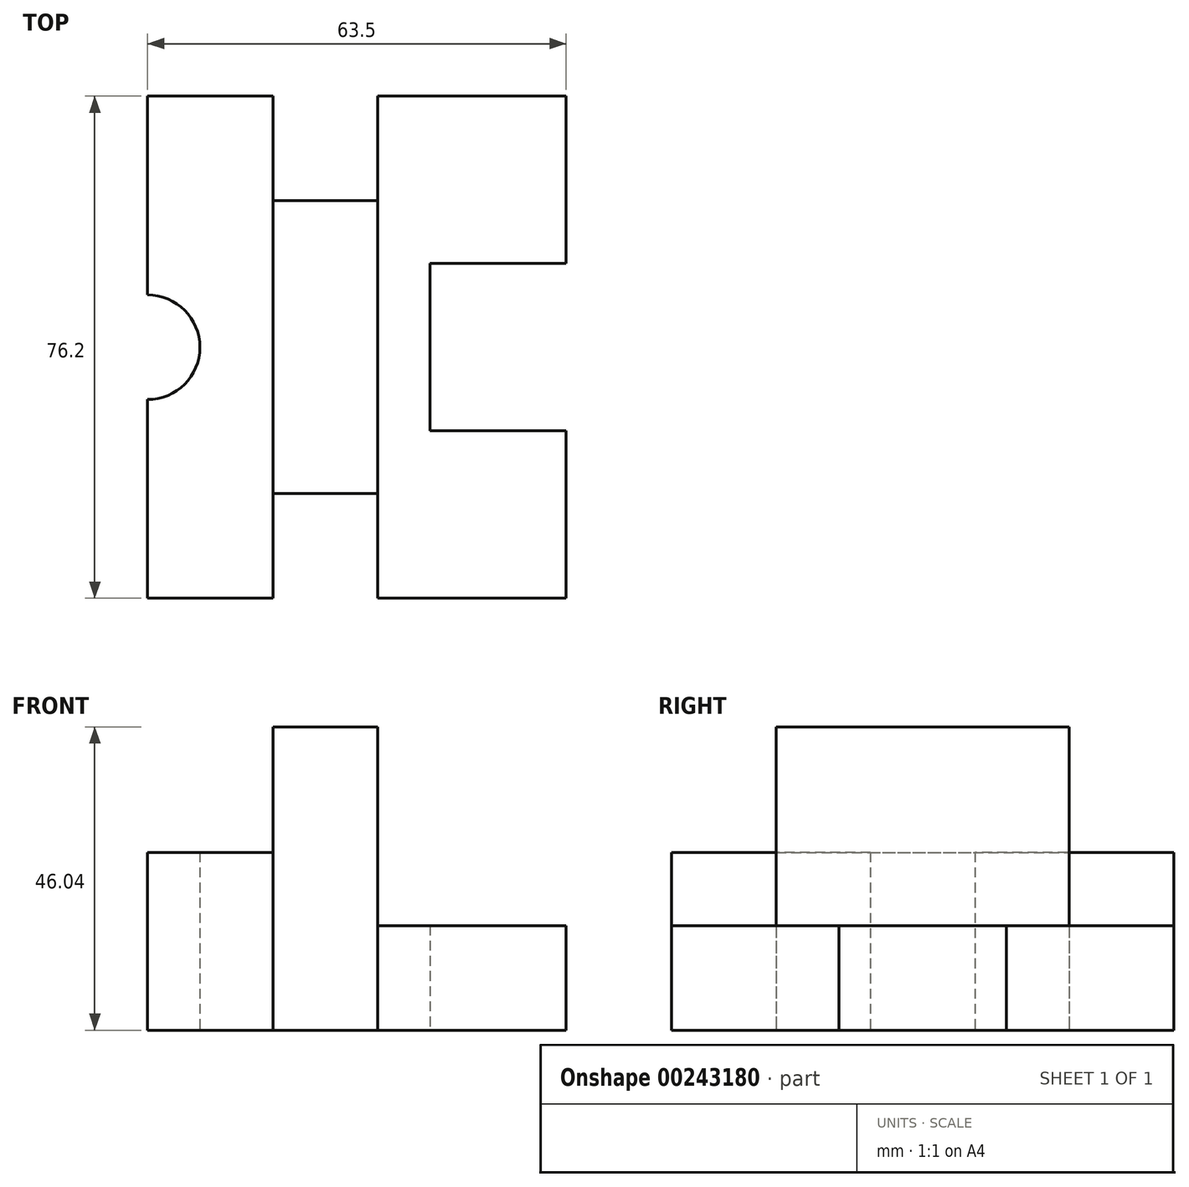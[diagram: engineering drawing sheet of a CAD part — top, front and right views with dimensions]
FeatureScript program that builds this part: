
annotation { "Feature Type Name" : "Feature", "Feature Type Description" : "" }
export const myFeature = defineFeature(function(context is Context, id is Id, definition is map)
    precondition{}
    {
        {
            var Q0;
            Q0=qCreatedBy(makeId("Top.planeOp"),FACE);
            var sketch = newSketch(context, id + "F0", { "sketchPlane" : qUnion([Q0])});
            skLineSegment(sketch, "E0", {"start": v(0, -15.88) * mm, "end": v(0, -76.2) * mm});
            skLineSegment(sketch, "E1", {"start": v(0, -76.2) * mm, "end": v(-127, -76.2) * mm});
            skLineSegment(sketch, "E2.bottom", {"start": v(-127, -76.2) * mm, "end": v(0, -76.2) * mm});
            skLineSegment(sketch, "E2.left", {"start": v(-127, -76.2) * mm, "end": v(-127, 0) * mm});
            skLineSegment(sketch, "E3.top", {"start": v(-127, -25.4) * mm, "end": v(-85.72, -25.4) * mm});
            skLineSegment(sketch, "E3.left", {"start": v(-127, 0) * mm, "end": v(-127, -25.4) * mm});
            skLineSegment(sketch, "E3.right", {"start": v(-85.72, 0) * mm, "end": v(-85.72, -25.4) * mm});
            skLineSegment(sketch, "E4", {"start": v(-69.85, -76.2) * mm, "end": v(-69.85, 0) * mm});
            skLineSegment(sketch, "E5", {"start": v(-69.85, -76.2) * mm, "end": v(-38.1, -76.2) * mm});
            skLineSegment(sketch, "E6", {"start": v(-38.1, -76.2) * mm, "end": v(-38.1, 0) * mm});
            skLineSegment(sketch, "E7", {"start": v(-38.1, -76.2) * mm, "end": v(-38.1, -44.45) * mm});
            skLineSegment(sketch, "E8", {"start": v(-38.1, -44.45) * mm, "end": v(-69.85, -44.45) * mm});
            skLineSegment(sketch, "E9.MirrorCS", {"start": v(0, 76.2) * mm, "end": v(-127, 76.2) * mm});
            skLineSegment(sketch, "E10.MirrorCS", {"start": v(0, 76.2) * mm, "end": v(0, 15.88) * mm});
            skLineSegment(sketch, "E11.MirrorCS", {"start": v(-127, 76.2) * mm, "end": v(0, 76.2) * mm});
            skLineSegment(sketch, "E12.MirrorCS", {"start": v(-127, 25.4) * mm, "end": v(-85.72, 25.4) * mm});
            skLineSegment(sketch, "E13.MirrorCS", {"start": v(-127, 0) * mm, "end": v(-127, 25.4) * mm});
            skLineSegment(sketch, "E14.MirrorCS", {"start": v(-85.72, 0) * mm, "end": v(-85.72, 25.4) * mm});
            skLineSegment(sketch, "E15.MirrorCS", {"start": v(-69.85, 76.2) * mm, "end": v(-69.85, 0) * mm});
            skLineSegment(sketch, "E16.MirrorCS", {"start": v(-69.85, 76.2) * mm, "end": v(-38.1, 76.2) * mm});
            skLineSegment(sketch, "E17.MirrorCS", {"start": v(-38.1, 76.2) * mm, "end": v(-38.1, 0) * mm});
            skLineSegment(sketch, "E18.MirrorCS", {"start": v(-38.1, 76.2) * mm, "end": v(-38.1, 44.45) * mm});
            skLineSegment(sketch, "E19.MirrorCS", {"start": v(-38.1, 44.45) * mm, "end": v(-69.85, 44.45) * mm});
            skLineSegment(sketch, "E20.MirrorCS", {"start": v(-127, 76.2) * mm, "end": v(-127, 0) * mm});
            skLineSegment(sketch, "E21.MirrorCS", {"start": v(0, -76.2) * mm, "end": v(127, -76.2) * mm});
            skLineSegment(sketch, "E22.MirrorCS", {"start": v(0, 15.88) * mm, "end": v(0, 76.2) * mm});
            skLineSegment(sketch, "E23.MirrorCS", {"start": v(127, 76.2) * mm, "end": v(0, 76.2) * mm});
            skLineSegment(sketch, "E24.MirrorCS", {"start": v(38.1, 76.2) * mm, "end": v(38.1, 44.45) * mm});
            skLineSegment(sketch, "E25.MirrorCS", {"start": v(127, 25.4) * mm, "end": v(85.72, 25.4) * mm});
            skLineSegment(sketch, "E26.MirrorCS", {"start": v(85.72, 0) * mm, "end": v(85.72, 25.4) * mm});
            skLineSegment(sketch, "E27.MirrorCS", {"start": v(69.85, 76.2) * mm, "end": v(38.1, 76.2) * mm});
            skLineSegment(sketch, "E28.MirrorCS", {"start": v(38.1, 76.2) * mm, "end": v(38.1, 0) * mm});
            skLineSegment(sketch, "E29.MirrorCS", {"start": v(38.1, 44.45) * mm, "end": v(69.85, 44.45) * mm});
            skLineSegment(sketch, "E30.MirrorCS", {"start": v(38.1, -44.45) * mm, "end": v(69.85, -44.45) * mm});
            skLineSegment(sketch, "E31.MirrorCS", {"start": v(38.1, -76.2) * mm, "end": v(38.1, -44.45) * mm});
            skLineSegment(sketch, "E32.MirrorCS", {"start": v(38.1, -76.2) * mm, "end": v(38.1, 0) * mm});
            skLineSegment(sketch, "E33.MirrorCS", {"start": v(69.85, -76.2) * mm, "end": v(38.1, -76.2) * mm});
            skLineSegment(sketch, "E34.MirrorCS", {"start": v(69.85, -76.2) * mm, "end": v(69.85, 0) * mm});
            skLineSegment(sketch, "E35.MirrorCS", {"start": v(85.72, 0) * mm, "end": v(85.72, -25.4) * mm});
            skLineSegment(sketch, "E36.MirrorCS", {"start": v(127, 0) * mm, "end": v(127, -25.4) * mm});
            skLineSegment(sketch, "E37.MirrorCS", {"start": v(127, -25.4) * mm, "end": v(85.72, -25.4) * mm});
            skLineSegment(sketch, "E38.MirrorCS", {"start": v(127, -76.2) * mm, "end": v(127, 0) * mm});
            skLineSegment(sketch, "E39.MirrorCS", {"start": v(127, -76.2) * mm, "end": v(0, -76.2) * mm});
            skLineSegment(sketch, "E40.MirrorCS", {"start": v(0, 76.2) * mm, "end": v(127, 76.2) * mm});
            skLineSegment(sketch, "E41.MirrorCS", {"start": v(127, 0) * mm, "end": v(127, 25.4) * mm});
            skLineSegment(sketch, "E42.MirrorCS", {"start": v(69.85, 76.2) * mm, "end": v(69.85, 0) * mm});
            skLineSegment(sketch, "E43.MirrorCS", {"start": v(127, 76.2) * mm, "end": v(127, 0) * mm});
            skCircle(sketch, "E44", {"center": v(0, 0) * mm, "radius": 15.88 * mm});
            skLineSegment(sketch, "E45.top", {"start": v(-38.1, -76.2) * mm, "end": v(-69.85, -76.2) * mm});
            skLineSegment(sketch, "E45.left", {"start": v(-38.1, -44.45) * mm, "end": v(-38.1, -76.2) * mm});
            skLineSegment(sketch, "E45.right", {"start": v(-69.85, -44.45) * mm, "end": v(-69.85, -76.2) * mm});
            skLineSegment(sketch, "E46.bottom", {"start": v(-69.85, -76.2) * mm, "end": v(-127, -76.2) * mm});
            skLineSegment(sketch, "E46.top", {"start": v(-69.85, 0) * mm, "end": v(-127, 0) * mm});
            skLineSegment(sketch, "E47.bottom", {"start": v(-127, 0) * mm, "end": v(-85.72, 0) * mm});
            skLineSegment(sketch, "E48.bottom", {"start": v(-85.72, 25.4) * mm, "end": v(-127, 25.4) * mm});
            skLineSegment(sketch, "E48.top", {"start": v(-85.72, -25.4) * mm, "end": v(-127, -25.4) * mm});
            skLineSegment(sketch, "E48.left", {"start": v(-85.72, 25.4) * mm, "end": v(-85.72, -25.4) * mm});
            skLineSegment(sketch, "E48.right", {"start": v(-127, 25.4) * mm, "end": v(-127, -25.4) * mm});
            skLineSegment(sketch, "E49.bottom", {"start": v(-127, 76.2) * mm, "end": v(-69.85, 76.2) * mm});
            skLineSegment(sketch, "E49.top", {"start": v(-127, 0) * mm, "end": v(-69.85, 0) * mm});
            skLineSegment(sketch, "E50.bottom", {"start": v(-69.85, -44.45) * mm, "end": v(-38.1, -44.45) * mm});
            skLineSegment(sketch, "E50.top", {"start": v(-69.85, 44.45) * mm, "end": v(-38.1, 44.45) * mm});
            skLineSegment(sketch, "E50.left", {"start": v(-69.85, -44.45) * mm, "end": v(-69.85, 44.45) * mm});
            skLineSegment(sketch, "E50.right", {"start": v(-38.1, -44.45) * mm, "end": v(-38.1, 44.45) * mm});
            skLineSegment(sketch, "E51.left", {"start": v(38.1, -44.45) * mm, "end": v(38.1, 44.45) * mm});
            skLineSegment(sketch, "E51.right", {"start": v(69.85, -44.45) * mm, "end": v(69.85, 44.45) * mm});
            skSolve(sketch);
        }
        {
            var Q0;
            {var subQ6=sQuery(id+"F0.wireOp",EDGE,"E48.bottom");Q0=makeQuery(id+"F0.imprint","IMPRINT",FACE,{"disambiguationData":[TD([[makeQuery(id+"F0.imprint","IMPRINT",EDGE,{"derivedFrom":subQ6}),-1.0]])]});}
            var Q1;
            Q1=makeQuery(id+"F0.imprint","IMPRINT",FACE,{"disambiguationData":[TD([[makeQuery(id+"F0.imprint","IMPRINT",EDGE,{"derivedFrom":sQuery(id+"F0.wireOp",EDGE,"E46.bottom")}),-1.0]])]});
            var Q2;
            {var subQ3=sQuery(id+"F0.wireOp",EDGE,"E50.bottom");Q2=makeQuery(id+"F0.imprint","IMPRINT",FACE,{"disambiguationData":[TD([[makeQuery(id+"F0.imprint","IMPRINT",EDGE,{"derivedFrom":subQ3}),1.0]])]});}
            var Q3;
            Q3=makeQuery(id+"F0.imprint","IMPRINT",FACE,{"disambiguationData":[TD([[makeQuery(id+"F0.imprint","IMPRINT",EDGE,{"derivedFrom":sQuery(id+"F0.wireOp",EDGE,"E2.bottom")}),1.0]])]});
            var Q4;
            Q4=makeQuery(id+"F0.imprint","IMPRINT",FACE,{"disambiguationData":[TD([[makeQuery(id+"F0.imprint","IMPRINT",EDGE,{"derivedFrom":sQuery(id+"F0.wireOp",EDGE,"E45.top")}),-1.0]])]});
            var Q5;
            Q5=makeQuery(id+"F0.imprint","IMPRINT",FACE,{"disambiguationData":[TD([[makeQuery(id+"F0.imprint","IMPRINT",EDGE,{"derivedFrom":sQuery(id+"F0.wireOp",EDGE,"E16.MirrorCS")}),-1.0]])]});
            var Q6;
            {var subQ3=sQuery(id+"F0.wireOp",EDGE,"E0");Q6=makeQuery(id+"F0.imprint","IMPRINT",FACE,{"disambiguationData":[TD([[makeQuery(id+"F0.imprint","IMPRINT",EDGE,{"derivedFrom":subQ3}),1.0]])]});}
            var Q7;
            {var subQ0=sQuery(id+"F0.wireOp",EDGE,"E32.MirrorCS");Q7=makeQuery(id+"F0.imprint","IMPRINT",FACE,{"disambiguationData":[TD([[makeQuery(id+"F0.imprint","IMPRINT",EDGE,{"derivedFrom":subQ0}),-1.0]])]});}
            var Q8;
            Q8=makeQuery(id+"F0.imprint","IMPRINT",FACE,{"disambiguationData":[TD([[makeQuery(id+"F0.imprint","IMPRINT",EDGE,{"derivedFrom":sQuery(id+"F0.wireOp",EDGE,"E30.MirrorCS")}),1.0]])]});
            var Q9;
            {var subQ1=sQuery(id+"F0.wireOp",EDGE,"E25.MirrorCS");Q9=makeQuery(id+"F0.imprint","IMPRINT",FACE,{"disambiguationData":[TD([[makeQuery(id+"F0.imprint","IMPRINT",EDGE,{"derivedFrom":subQ1}),-1.0]])]});}
            var Q10;
            {var subQ0=sQuery(id+"F0.wireOp",EDGE,"E28.MirrorCS");Q10=makeQuery(id+"F0.imprint","IMPRINT",FACE,{"disambiguationData":[TD([[makeQuery(id+"F0.imprint","IMPRINT",EDGE,{"derivedFrom":subQ0}),1.0]])]});}
            extrude(context, id + "F1", {"entities" : qUnion([Q0, Q1, Q2, Q3, Q4, Q5, Q6, Q7, Q8, Q9, Q10]), "depth" : 31.75 * mm});
        }
        {
            var Q0;
            Q0=makeQuery(id+"F0.imprint","IMPRINT",FACE,{"disambiguationData":[TD([[makeQuery(id+"F0.imprint","IMPRINT",EDGE,{"derivedFrom":sQuery(id+"F0.wireOp",EDGE,"E16.MirrorCS")}),-1.0]])]});
            var Q1;
            Q1=makeQuery(id+"F0.imprint","IMPRINT",FACE,{"disambiguationData":[TD([[makeQuery(id+"F0.imprint","IMPRINT",EDGE,{"derivedFrom":sQuery(id+"F0.wireOp",EDGE,"E45.top")}),-1.0]])]});
            var Q2;
            {var subQ0=sQuery(id+"F0.wireOp",EDGE,"E32.MirrorCS");Q2=makeQuery(id+"F0.imprint","IMPRINT",FACE,{"disambiguationData":[TD([[makeQuery(id+"F0.imprint","IMPRINT",EDGE,{"derivedFrom":subQ0}),-1.0]])]});}
            var Q3;
            {var subQ0=sQuery(id+"F0.wireOp",EDGE,"E28.MirrorCS");Q3=makeQuery(id+"F0.imprint","IMPRINT",FACE,{"disambiguationData":[TD([[makeQuery(id+"F0.imprint","IMPRINT",EDGE,{"derivedFrom":subQ0}),1.0]])]});}
            extrude(context, id + "F2", {"entities" : qUnion([Q0, Q1, Q2, Q3]), "operationType" : NewBodyOperationType.ADD, "depth" : 92.07 * mm});
        }
        {
            var Q0;
            {var subQ3=sQuery(id+"F0.wireOp",EDGE,"E0");Q0=makeQuery(id+"F0.imprint","IMPRINT",FACE,{"disambiguationData":[TD([[makeQuery(id+"F0.imprint","IMPRINT",EDGE,{"derivedFrom":subQ3}),1.0]])]});}
            var Q1;
            Q1=makeQuery(id+"F0.imprint","IMPRINT",FACE,{"disambiguationData":[TD([[makeQuery(id+"F0.imprint","IMPRINT",EDGE,{"derivedFrom":sQuery(id+"F0.wireOp",EDGE,"E2.bottom")}),1.0]])]});
            extrude(context, id + "F3", {"entities" : qUnion([Q0, Q1]), "operationType" : NewBodyOperationType.ADD, "depth" : 53.97 * mm});
        }
        {
            var Q0;
            Q0=makeQuery(id+"F0.imprint","IMPRINT",FACE,{"disambiguationData":[TD([[makeQuery(id+"F0.imprint","IMPRINT",EDGE,{"derivedFrom":sQuery(id+"F0.wireOp",EDGE,"E30.MirrorCS")}),1.0]])]});
            var Q1;
            {var subQ3=sQuery(id+"F0.wireOp",EDGE,"E50.bottom");Q1=makeQuery(id+"F0.imprint","IMPRINT",FACE,{"disambiguationData":[TD([[makeQuery(id+"F0.imprint","IMPRINT",EDGE,{"derivedFrom":subQ3}),1.0]])]});}
            extrude(context, id + "F4", {"entities" : qUnion([Q0, Q1]), "operationType" : NewBodyOperationType.ADD, "depth" : 73.02 * mm});
        }
        {
            var Q0;
            Q0=makeQuery(id+"F1.opExtrude","SWEPT_BODY",BODY,{"disambiguationData":[OSD([sQuery(id+"F0.wireOp",EDGE,"E2.bottom"),sQuery(id+"F0.wireOp",EDGE,"E11.MirrorCS"),sQuery(id+"F0.wireOp",EDGE,"E16.MirrorCS"),sQuery(id+"F0.wireOp",EDGE,"E25.MirrorCS"),sQuery(id+"F0.wireOp",EDGE,"E26.MirrorCS"),sQuery(id+"F0.wireOp",EDGE,"E35.MirrorCS"),sQuery(id+"F0.wireOp",EDGE,"E37.MirrorCS"),sQuery(id+"F0.wireOp",EDGE,"E38.MirrorCS"),sQuery(id+"F0.wireOp",EDGE,"E39.MirrorCS"),sQuery(id+"F0.wireOp",EDGE,"E40.MirrorCS"),sQuery(id+"F0.wireOp",EDGE,"E43.MirrorCS"),sQuery(id+"F0.wireOp",EDGE,"E44"),sQuery(id+"F0.wireOp",EDGE,"E45.top"),sQuery(id+"F0.wireOp",EDGE,"E46.bottom"),sQuery(id+"F0.wireOp",EDGE,"E2.left"),sQuery(id+"F0.wireOp",EDGE,"E48.bottom"),sQuery(id+"F0.wireOp",EDGE,"E48.top"),sQuery(id+"F0.wireOp",EDGE,"E48.left"),sQuery(id+"F0.wireOp",EDGE,"E49.bottom"),sQuery(id+"F0.wireOp",EDGE,"E20.MirrorCS")])]});
            var Q1;
            Q1=qCreatedBy(makeId("Origin.pointOp"),VERTEX);
            transform(context, id + "F5", {"entities" : qUnion([Q0]), "transformType" : TransformType.SCALE_UNIFORMLY, "scale" : 0.5, "scalePoint" : qUnion([Q1]), "makeCopy" : false});
        }
    });
